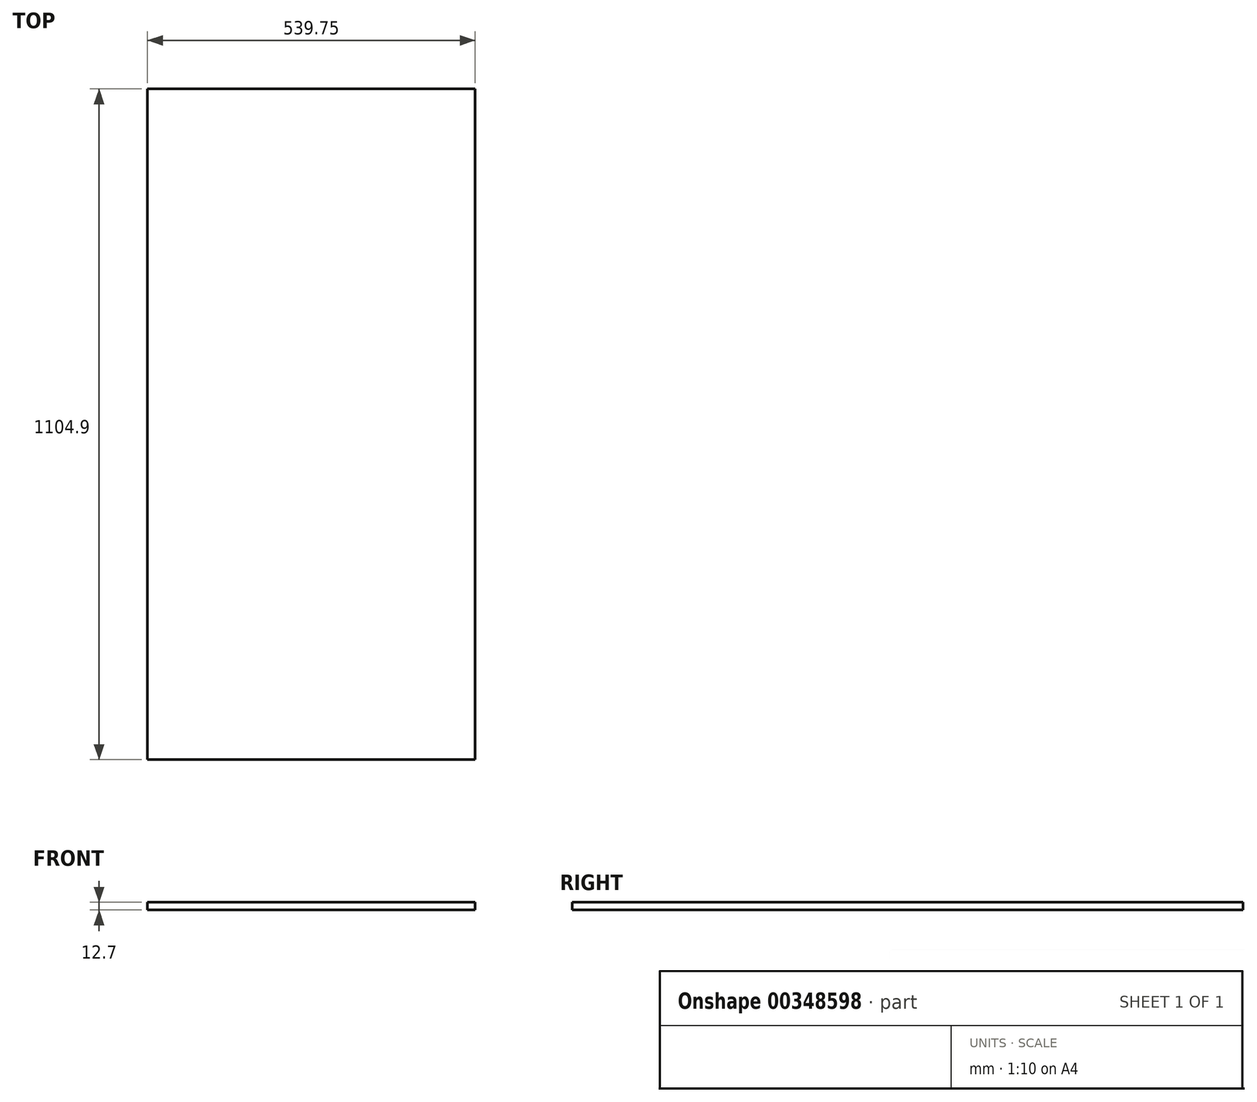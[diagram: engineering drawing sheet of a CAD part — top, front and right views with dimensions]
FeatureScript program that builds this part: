
annotation { "Feature Type Name" : "Feature", "Feature Type Description" : "" }
export const myFeature = defineFeature(function(context is Context, id is Id, definition is map)
    precondition{}
    {
        {
            var Q0;
            Q0=qCreatedBy(makeId("Top.planeOp"),FACE);
            var sketch = newSketch(context, id + "F0", { "sketchPlane" : qUnion([Q0])});
            skLineSegment(sketch, "E0.bottom", {"start": v(-265.33, 983.37) * mm, "end": v(274.42, 983.37) * mm});
            skLineSegment(sketch, "E0.top", {"start": v(-265.33, -121.53) * mm, "end": v(274.42, -121.53) * mm});
            skLineSegment(sketch, "E0.left", {"start": v(-265.33, 983.37) * mm, "end": v(-265.33, -121.53) * mm});
            skLineSegment(sketch, "E0.right", {"start": v(274.42, 983.37) * mm, "end": v(274.42, -121.53) * mm});
            skSolve(sketch);
        }
        {
            var Q0;
            Q0=qSketchRegion(id+"F0",true);
            extrude(context, id + "F1", {"entities" : qUnion([Q0]), "depth" : 12.7 * mm});
        }
    });
